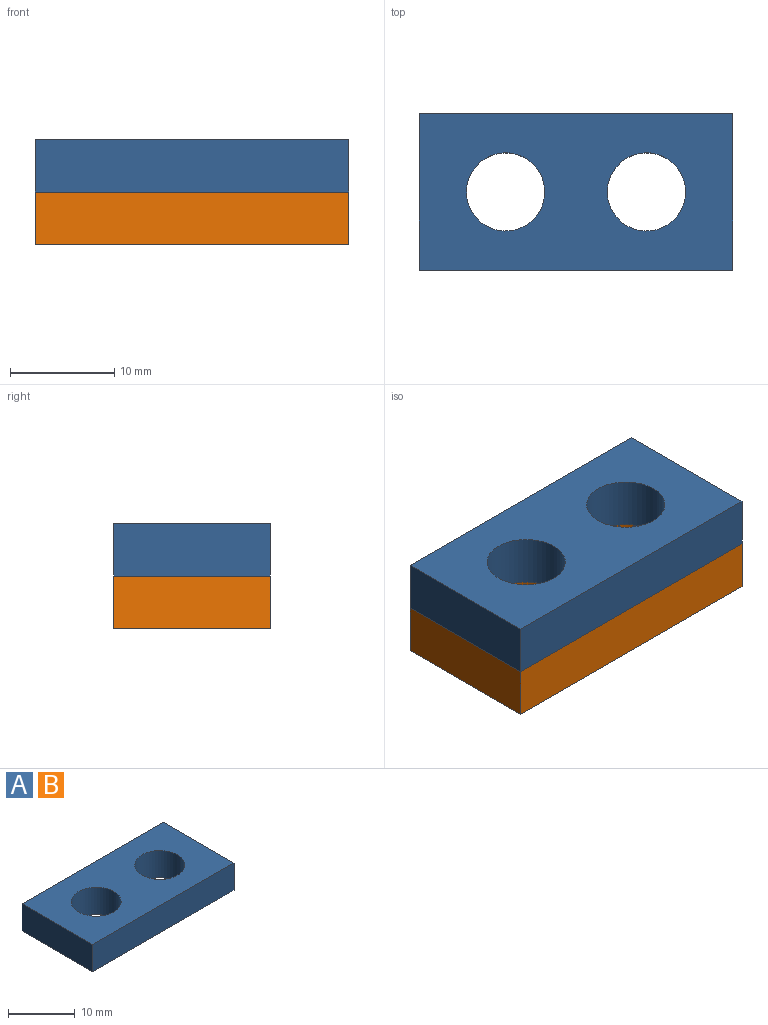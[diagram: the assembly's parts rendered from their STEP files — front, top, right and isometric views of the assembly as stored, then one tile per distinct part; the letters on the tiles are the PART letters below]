
ASSEMBLY  parts=2 mates=1
PART A: 8 faces, bbox 30x15x5 mm
  f0: plane 30x5mm, normal (0,1,0), area 150mm2, adj f1,f5,f6,f7
  f1: plane 15x5mm, normal (-1,0,0), area 75mm2, adj f0,f2,f6,f7
  f2: plane 30x5mm, normal (0,-1,0), area 150mm2, adj f1,f5,f6,f7
  f3: cylinder r=3.75mm len=7.5mm, axis (0,0,-1), area 117.8mm2, adj f6,f7
  f4: cylinder r=3.75mm len=7.5mm, axis (0,0,-1), area 117.8mm2, adj f6,f7
  f5: plane 15x5mm, normal (1,0,0), area 75mm2, adj f0,f2,f6,f7
  f6: plane 30x15mm, normal (0,0,1), area 361.6mm2, adj f0,f1,f2,f3,f4,f5
  f7: plane 30x15mm, normal (0,0,-1), area 361.6mm2, adj f0,f1,f2,f3,f4,f5
PART B: same geometry as A
PLACE A t=(-1.99,3.75,4.85)mm
PLACE B t=(-1.99,3.75,-0.15)mm
MATE fastened B.f6 <-> A.f7  axis (0,0,1) through (-16.99,-3.75,4.85)mm
